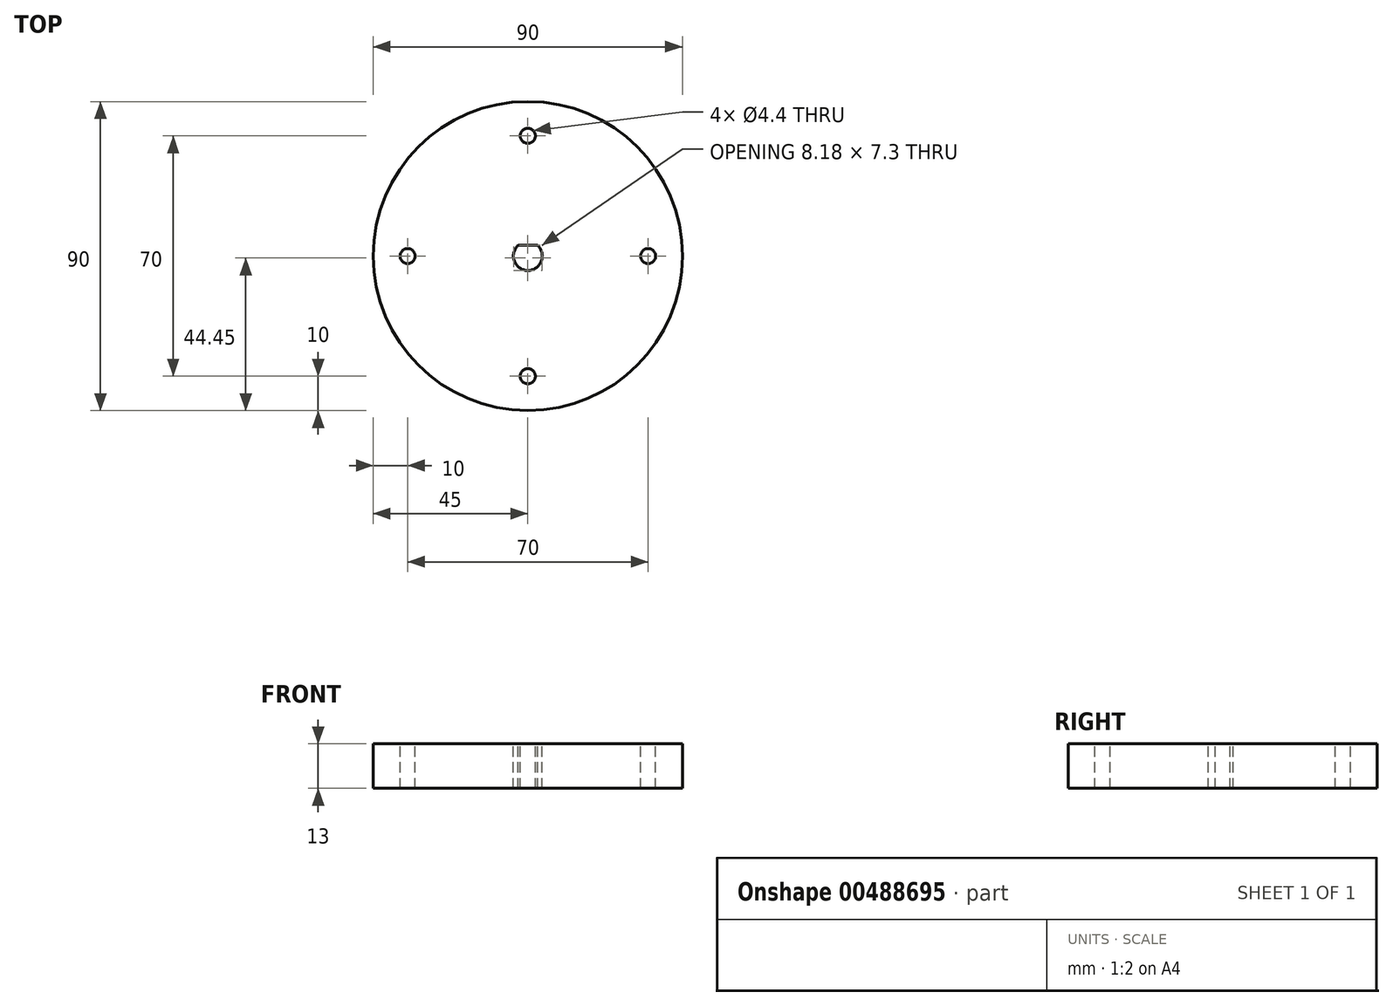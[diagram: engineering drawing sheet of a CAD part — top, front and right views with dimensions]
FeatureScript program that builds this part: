
annotation { "Feature Type Name" : "Feature", "Feature Type Description" : "" }
export const myFeature = defineFeature(function(context is Context, id is Id, definition is map)
    precondition{}
    {
        {
            var Q0;
            Q0=qCreatedBy(makeId("Top.planeOp"),FACE);
            var sketch = newSketch(context, id + "F0", { "sketchPlane" : qUnion([Q0])});
            skCircle(sketch, "E0", {"center": v(0, 0) * mm, "radius": 45 * mm});
            skSolve(sketch);
        }
        {
            var Q0;
            Q0=qSketchRegion(id+"F0",true);
            extrude(context, id + "F1", {"entities" : qUnion([Q0]), "depth" : 13 * mm, "offsetDistance" : 25 * mm});
        }
        {
            var Q0;
            Q0=makeQuery(id+"F1.opExtrude","CAP_FACE",FACE,{"disambiguationData":[OSD([sQuery(id+"F0.wireOp",EDGE,"E0")])],"isStart":false});
            var sketch = newSketch(context, id + "F2", { "sketchPlane" : qUnion([Q0])});
            skArc(sketch, "E1", {"start": v(-2.83, 3.1) * mm, "mid": v(0, -4.2) * mm, "end": v(2.83, 3.1) * mm});
            skLineSegment(sketch, "E2", {"start": v(-2.83, 3.1) * mm, "end": v(2.83, 3.1) * mm});
            skSolve(sketch);
        }
        {
            var Q0;
            Q0=qSketchRegion(id+"F2",true);
            extrude(context, id + "F3", {"entities" : qUnion([Q0]), "operationType" : NewBodyOperationType.REMOVE, "oppositeDirection" : true, "depth" : 16 * mm});
        }
        {
            var Q0;
            Q0=makeQuery(id+"F1.opExtrude","CAP_FACE",FACE,{"disambiguationData":[OSD([sQuery(id+"F0.wireOp",EDGE,"E0")])],"isStart":false});
            var sketch = newSketch(context, id + "F4", { "sketchPlane" : qUnion([Q0])});
            skCircle(sketch, "E3", {"center": v(0, 0) * mm, "radius": 35 * mm, "construction": true});
            skCircle(sketch, "E4", {"center": v(0, 35) * mm, "radius": 2.2 * mm});
            skCircle(sketch, "E5", {"center": v(35, 0) * mm, "radius": 2.2 * mm});
            skCircle(sketch, "E6", {"center": v(-35, 0) * mm, "radius": 2.2 * mm});
            skCircle(sketch, "E7", {"center": v(0, -35) * mm, "radius": 2.2 * mm});
            skSolve(sketch);
        }
        {
            var Q0;
            Q0=qSketchRegion(id+"F4",true);
            extrude(context, id + "F5", {"entities" : qUnion([Q0]), "operationType" : NewBodyOperationType.REMOVE, "oppositeDirection" : true, "depth" : 14 * mm, "offsetDistance" : 25 * mm});
        }
    });
